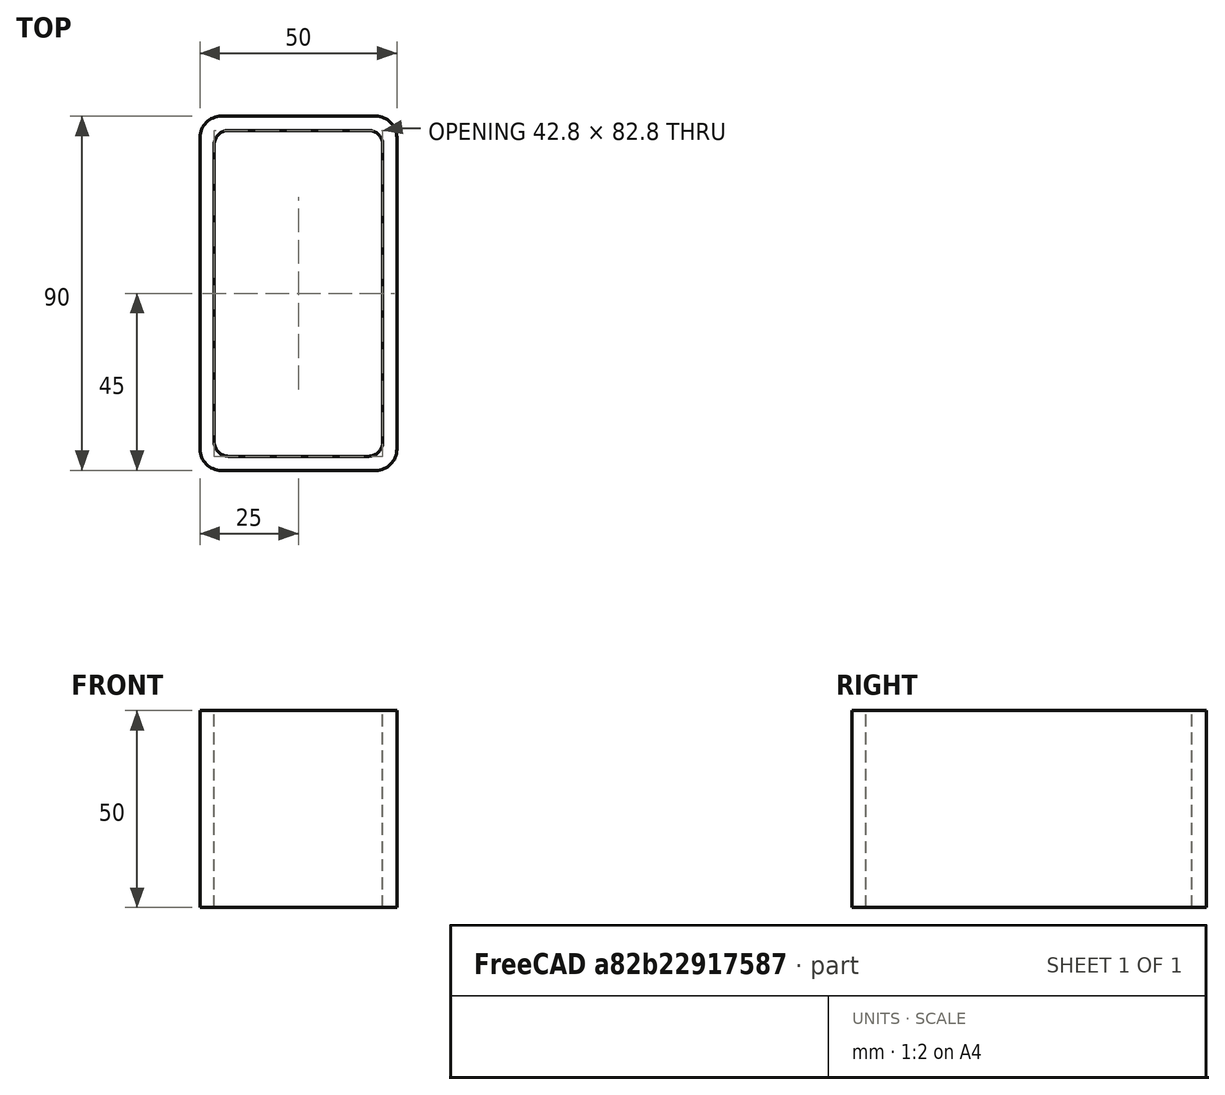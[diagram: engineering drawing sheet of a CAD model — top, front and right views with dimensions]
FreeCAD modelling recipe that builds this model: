
FCSTD DOCUMENT  (FreeCAD 0.15R4671 (Git))
Label: Rectangular hollow section 90x50x3.6 EN10219 S235JRH
License: All rights reserved
LicenseURL: http://en.wikipedia.org/wiki/All_rights_reserved
objects: Sketcher::SketchObject×1, Part::Extrusion×1
note: 2 computed .brp shape members not serialized (recipe doc carries the construction recipe); baked Part::Feature solids carry a one-line shape summary decoded from their .brp

FEATURE [Sketcher::SketchObject] Sketch
  sketch-geometry (16):
    g0: LineSegment StartX=-17.8 StartY=41.4 StartZ=0 EndX=17.8 EndY=41.4 EndZ=0
    g1: LineSegment StartX=21.4 StartY=37.8 StartZ=0 EndX=21.4 EndY=-37.8 EndZ=0
    g2: LineSegment StartX=17.8 StartY=-41.4 StartZ=0 EndX=-17.8 EndY=-41.4 EndZ=0
    g3: LineSegment StartX=-21.4 StartY=-37.8 StartZ=0 EndX=-21.4 EndY=37.8 EndZ=0
    g4: LineSegment StartX=-19.6 StartY=45 StartZ=0 EndX=19.6 EndY=45 EndZ=0
    g5: LineSegment StartX=25 StartY=39.6 StartZ=0 EndX=25 EndY=-39.6 EndZ=0
    g6: LineSegment StartX=19.6 StartY=-45 StartZ=0 EndX=-19.6 EndY=-45 EndZ=0
    g7: LineSegment StartX=-25 StartY=-39.6 StartZ=0 EndX=-25 EndY=39.6 EndZ=0
    g8: ArcOfCircle CenterX=-17.8 CenterY=37.8 CenterZ=0 NormalX=0 NormalY=0 NormalZ=1 Radius=3.6 StartAngle=1.5708 EndAngle=3.14159
    g9: ArcOfCircle CenterX=17.8 CenterY=37.8 CenterZ=0 NormalX=0 NormalY=0 NormalZ=1 Radius=3.6 StartAngle=0 EndAngle=1.5708
    g10: ArcOfCircle CenterX=17.8 CenterY=-37.8 CenterZ=0 NormalX=0 NormalY=0 NormalZ=1 Radius=3.6 StartAngle=4.71239 EndAngle=6.28319
    g11: ArcOfCircle CenterX=-17.8 CenterY=-37.8 CenterZ=0 NormalX=0 NormalY=0 NormalZ=1 Radius=3.6 StartAngle=3.14159 EndAngle=4.71239
    g12: ArcOfCircle CenterX=19.6 CenterY=39.6 CenterZ=0 NormalX=0 NormalY=0 NormalZ=1 Radius=5.4 StartAngle=0 EndAngle=1.5708
    g13: ArcOfCircle CenterX=19.6 CenterY=-39.6 CenterZ=0 NormalX=0 NormalY=0 NormalZ=1 Radius=5.4 StartAngle=4.71239 EndAngle=6.28319
    g14: ArcOfCircle CenterX=-19.6 CenterY=-39.6 CenterZ=0 NormalX=0 NormalY=0 NormalZ=1 Radius=5.4 StartAngle=3.14159 EndAngle=4.71239
    g15: ArcOfCircle CenterX=-19.6 CenterY=39.6 CenterZ=0 NormalX=0 NormalY=0 NormalZ=1 Radius=5.4 StartAngle=1.5708 EndAngle=3.14159
  constraints (36):
    c: Horizontal(g2)
    c: Vertical(g3)
    c: Horizontal(g6)
    c: Vertical(g7)
    c: Tangent(g3,g8) = 1.5708
    c: Tangent(g0,g8) = 1.5708
    c: Tangent(g0,g9) = 1.5708
    c: Tangent(g1,g9) = 1.5708
    c: Tangent(g1,g10) = 1.5708
    c: Tangent(g2,g10) = 1.5708
    c: Tangent(g2,g11) = 1.5708
    c: Tangent(g3,g11) = 1.5708
    c: Tangent(g4,g12) = 1.5708
    c: Tangent(g5,g12) = 1.5708
    c: Tangent(g5,g13) = 1.5708
    c: Tangent(g6,g13) = 1.5708
    c: Tangent(g6,g14) = 1.5708
    c: Tangent(g7,g14) = 1.5708
    c: Tangent(g7,g15) = 1.5708
    c: Tangent(g4,g15) = 1.5708
    c: Equal(g9,g8)
    c: Equal(g9,g11)
    c: Equal(g9,g10)
    c: Equal(g12,g15)
    c: Equal(g12,g14)
    c: Equal(g12,g13)
    c: Symmetric(g4,g6,g-1)
    c: Symmetric(g7,g5,g-2)
    c: DistanceY(g4,g6) = -90
    c: DistanceX(g7,g5) = 50
    c: Symmetric(g3,g1,g-2)
    c: Symmetric(g0,g2,g-1)
    c: DistanceY(g0,g4) = 3.6
    c: DistanceX(g5,g1) = -3.6
    c: Radius(g9) = 3.6
    c: Radius(g12) = 5.4
FEATURE [Part::Extrusion] Extrude  label="Rectangular hollow section 90x50x3.6 EN10219 S235JRH"
  Base = -> Sketch
  Dir = (0,0,50)
  Solid = true
